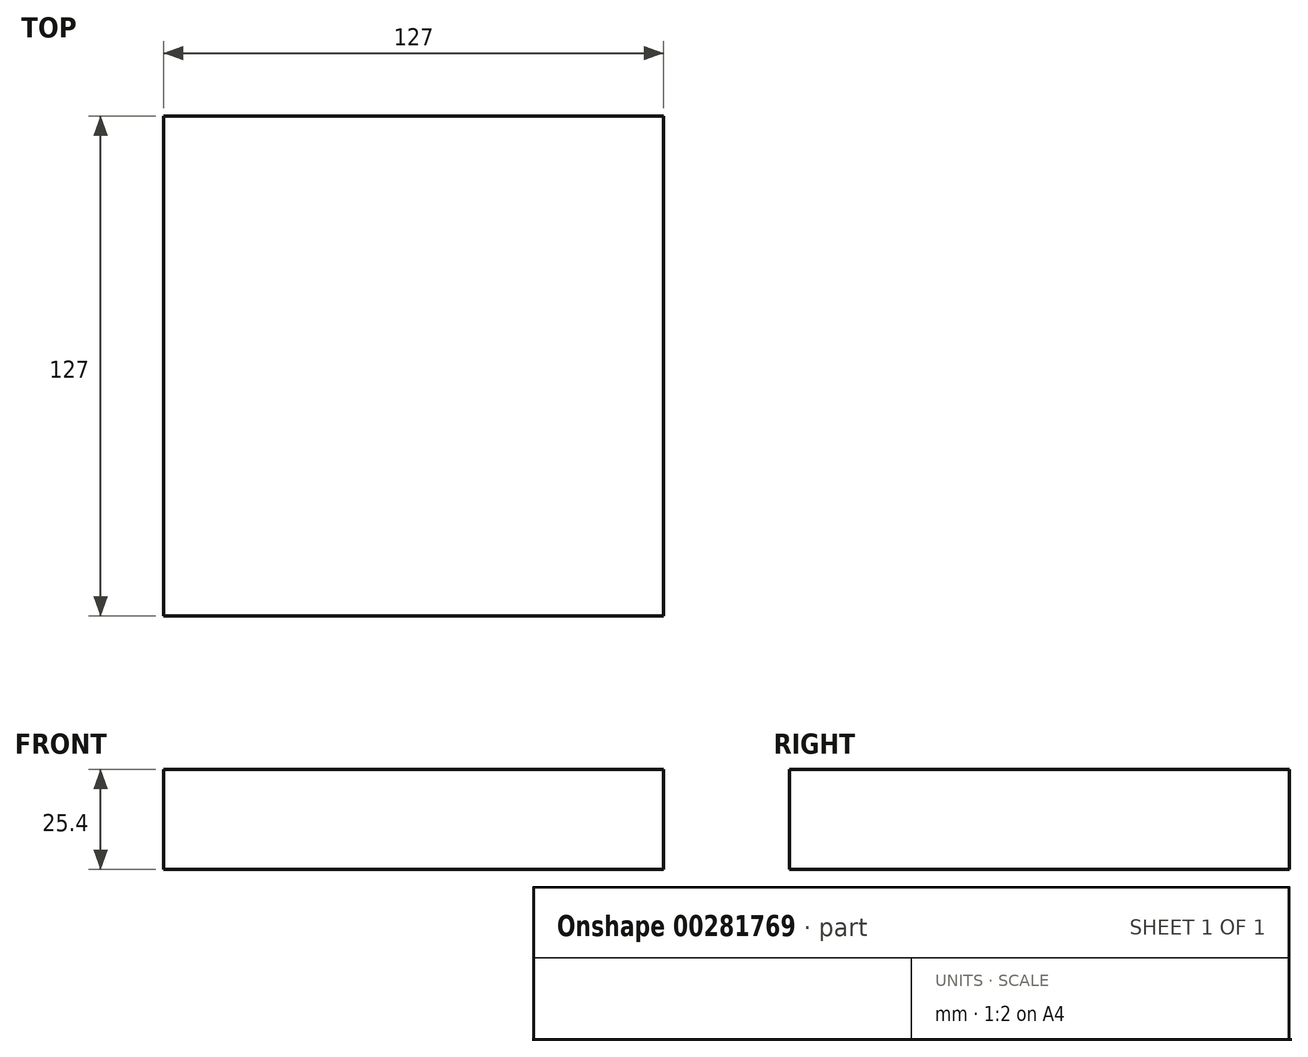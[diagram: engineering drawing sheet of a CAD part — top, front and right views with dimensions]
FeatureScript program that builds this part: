
annotation { "Feature Type Name" : "Feature", "Feature Type Description" : "" }
export const myFeature = defineFeature(function(context is Context, id is Id, definition is map)
    precondition{}
    {
        {
            var Q0;
            Q0=qCreatedBy(makeId("Top.planeOp"),FACE);
            var sketch = newSketch(context, id + "F0", { "sketchPlane" : qUnion([Q0])});
            skLineSegment(sketch, "E0.bottom", {"start": v(-63.5, 63.5) * mm, "end": v(63.5, 63.5) * mm});
            skLineSegment(sketch, "E0.top", {"start": v(-63.5, -63.5) * mm, "end": v(63.5, -63.5) * mm});
            skLineSegment(sketch, "E0.left", {"start": v(-63.5, 63.5) * mm, "end": v(-63.5, -63.5) * mm});
            skLineSegment(sketch, "E0.right", {"start": v(63.5, 63.5) * mm, "end": v(63.5, -63.5) * mm});
            skPoint(sketch, "E0.middle", {"position": v(0, 0) * mm});
            skSolve(sketch);
        }
        {
            var Q0;
            Q0 = qSketchRegion(id + "F0", true);
            extrude(context, id + "F1", {"entities" : qUnion([Q0]), "depth" : 25.4 * mm});
        }
    });
